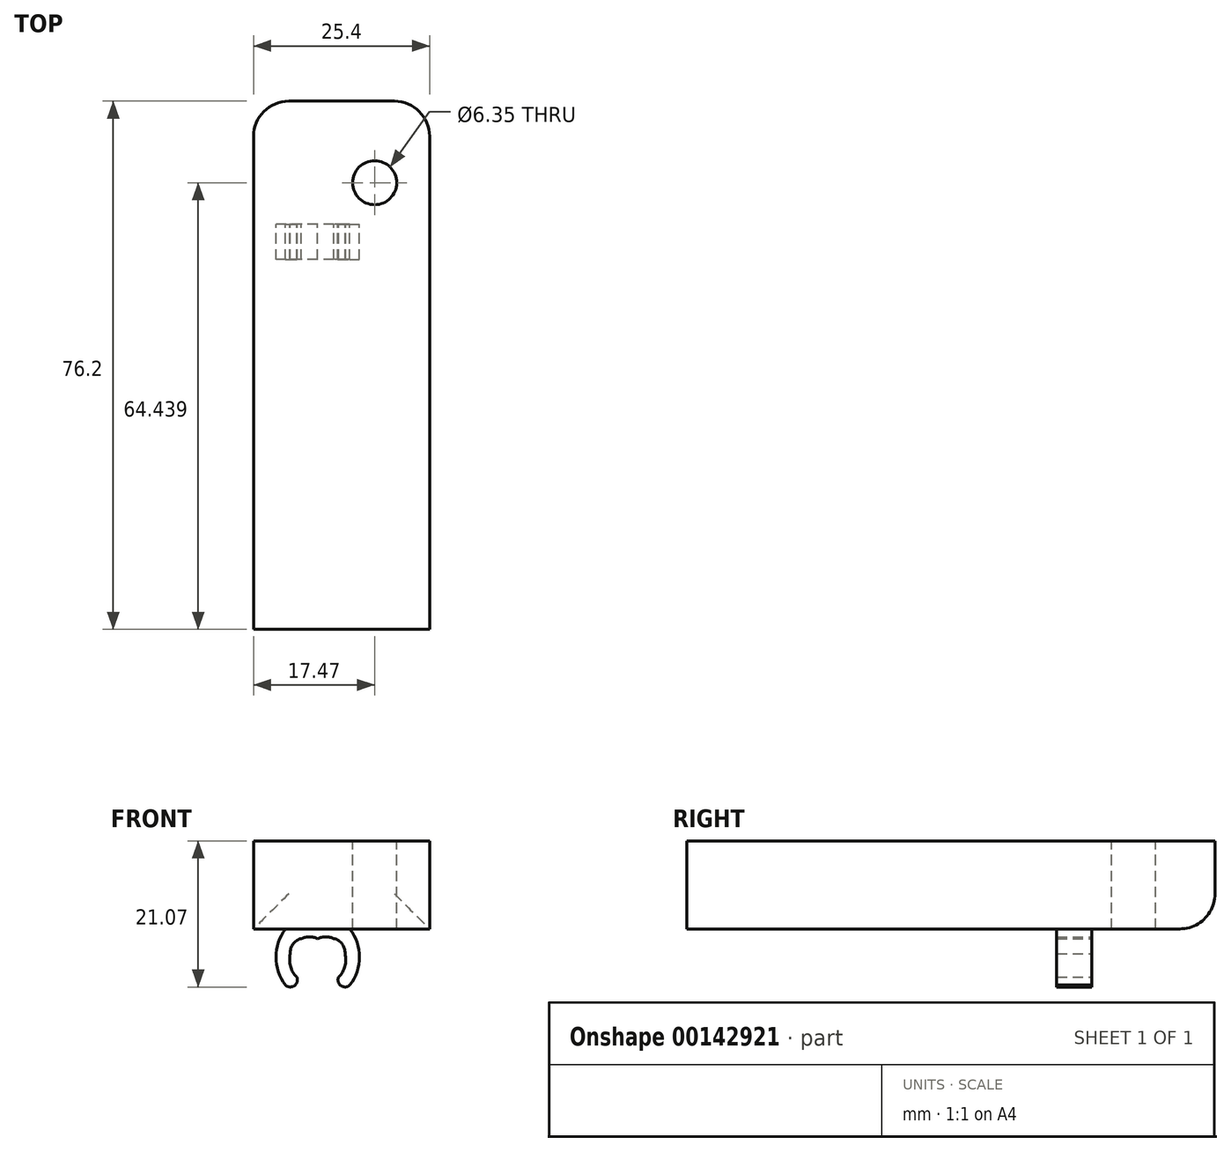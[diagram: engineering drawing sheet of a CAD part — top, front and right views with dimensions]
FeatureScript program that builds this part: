
annotation { "Feature Type Name" : "Feature", "Feature Type Description" : "" }
export const myFeature = defineFeature(function(context is Context, id is Id, definition is map)
    precondition{}
    {
        {
            var Q0;
            Q0=qCreatedBy(makeId("Top.planeOp"),FACE);
            var sketch = newSketch(context, id + "F0", { "sketchPlane" : qUnion([Q0])});
            skLineSegment(sketch, "E0.bottom", {"start": v(0, 17.76) * mm, "end": v(25.4, 17.76) * mm});
            skLineSegment(sketch, "E0.top", {"start": v(0, -58.44) * mm, "end": v(25.4, -58.44) * mm});
            skLineSegment(sketch, "E0.left", {"start": v(0, 17.76) * mm, "end": v(0, -58.44) * mm});
            skLineSegment(sketch, "E0.right", {"start": v(25.4, 17.76) * mm, "end": v(25.4, -58.44) * mm});
            skSolve(sketch);
        }
        {
            var Q0;
            Q0=makeQuery(id+"F0.imprint","IMPRINT",FACE,{"disambiguationData":[TD([[makeQuery(id+"F0.imprint","IMPRINT",EDGE,{"derivedFrom":sQuery(id+"F0.wireOp",EDGE,"E0.bottom")}),-1.0]])]});
            extrude(context, id + "F1", {"entities" : qUnion([Q0]), "depth" : 12.7 * mm});
        }
        {
            var Q0;
            Q0=makeQuery(id+"F1.opExtrude","CAP_FACE",FACE,{"disambiguationData":[OSD([sQuery(id+"F0.wireOp",EDGE,"E0.bottom"),sQuery(id+"F0.wireOp",EDGE,"E0.top"),sQuery(id+"F0.wireOp",EDGE,"E0.left"),sQuery(id+"F0.wireOp",EDGE,"E0.right")])],"isStart":false});
            var sketch = newSketch(context, id + "F2", { "sketchPlane" : qUnion([Q0])});
            skCircle(sketch, "E1", {"center": v(17.47, 6) * mm, "radius": 3.18 * mm});
            skSolve(sketch);
        }
        {
            var Q0;
            Q0=sQuery(id+"F2.wireOp",VERTEX,"E1.center");
            var Q1;
            Q1=makeQuery(id+"F1.opExtrude","SWEPT_BODY",BODY,{"disambiguationData":[OSD([sQuery(id+"F0.wireOp",EDGE,"E0.bottom"),sQuery(id+"F0.wireOp",EDGE,"E0.top"),sQuery(id+"F0.wireOp",EDGE,"E0.left"),sQuery(id+"F0.wireOp",EDGE,"E0.right")])]});
            hole(context, id + "F3", {"style" : HoleStyle.SIMPLE, "endStyle" : HoleEndStyle.THROUGH, "holeDiameter" : 6.35 * mm, "locations" : qUnion([Q0]), "scope" : qUnion([Q1]), "isTappedThrough" : true});
        }
        {
            var Q0;
            Q0=qCreatedBy(makeId("Front.planeOp"),FACE);
            var sketch = newSketch(context, id + "F4", { "sketchPlane" : qUnion([Q0])});
            skLineSegment(sketch, "E2", {"start": v(9.25, 8.3) * mm, "end": v(9.25, -9.6) * mm, "construction": true});
            skLineSegment(sketch, "E3", {"start": v(9.25, 0) * mm, "end": v(13.89, 0) * mm});
            skArc(sketch, "E4", {"start": v(13.89, -8.1) * mm, "mid": v(15.27, -4.05) * mm, "end": v(13.89, 0) * mm});
            skArc(sketch, "E5", {"start": v(12.25, -6.95) * mm, "mid": v(12.61, -8.19) * mm, "end": v(13.89, -8.1) * mm});
            skArc(sketch, "E6", {"start": v(12.25, -6.95) * mm, "mid": v(13.17, -5.39) * mm, "end": v(13.2, -3.57) * mm});
            skArc(sketch, "E7", {"start": v(13.2, -3.57) * mm, "mid": v(12.8, -2.18) * mm, "end": v(11.6, -1.39) * mm});
            skArc(sketch, "E8", {"start": v(11.6, -1.39) * mm, "mid": v(10.42, -1.14) * mm, "end": v(9.25, -1.39) * mm});
            skArc(sketch, "E9.MirrorCS", {"start": v(6.25, -6.95) * mm, "mid": v(5.33, -5.39) * mm, "end": v(5.3, -3.57) * mm});
            skArc(sketch, "E10.MirrorCS", {"start": v(6.9, -1.39) * mm, "mid": v(8.07, -1.14) * mm, "end": v(9.25, -1.39) * mm});
            skArc(sketch, "E11.MirrorCS", {"start": v(4.6, -8.1) * mm, "mid": v(3.23, -4.05) * mm, "end": v(4.6, 0) * mm});
            skArc(sketch, "E12.MirrorCS", {"start": v(6.25, -6.95) * mm, "mid": v(5.89, -8.19) * mm, "end": v(4.6, -8.1) * mm});
            skLineSegment(sketch, "E13.MirrorCS", {"start": v(9.25, 0) * mm, "end": v(4.6, 0) * mm});
            skArc(sketch, "E14.MirrorCS", {"start": v(5.3, -3.57) * mm, "mid": v(5.7, -2.18) * mm, "end": v(6.9, -1.39) * mm});
            skSolve(sketch);
        }
        {
            var Q0;
            Q0=makeQuery(id+"F4.imprint","IMPRINT",FACE,{"disambiguationData":[TD([[makeQuery(id+"F4.imprint","IMPRINT",EDGE,{"derivedFrom":sQuery(id+"F4.wireOp",EDGE,"E3")}),-1.0]])]});
            extrude(context, id + "F5", {"entities" : qUnion([Q0]), "operationType" : NewBodyOperationType.ADD, "depth" : 5.08 * mm});
        }
        {
            var Q0;
            Q0=makeQuery(id+"F1.opExtrude","SWEPT_EDGE",EDGE,{"disambiguationData":[OSD([sQuery(id+"F0.wireOp",EDGE,"E0.bottom"),sQuery(id+"F0.wireOp",EDGE,"E0.left")])]});
            var Q1;
            Q1=makeQuery(id+"F1.opExtrude","SWEPT_EDGE",EDGE,{"disambiguationData":[OSD([sQuery(id+"F0.wireOp",EDGE,"E0.bottom"),sQuery(id+"F0.wireOp",EDGE,"E0.right")])]});
            var Q2;
            Q2=makeQuery(id+"F1.opExtrude","CAP_EDGE",EDGE,{"disambiguationData":[OSD([sQuery(id+"F0.wireOp",EDGE,"E0.bottom")])],"isStart":true});
            fillet(context, id + "F6", {"entities" : qUnion([Q0, Q1, Q2]), "radius" : 5.08 * mm, "tangentPropagation" : true, "allowEdgeOverflow" : false});
        }
    });
